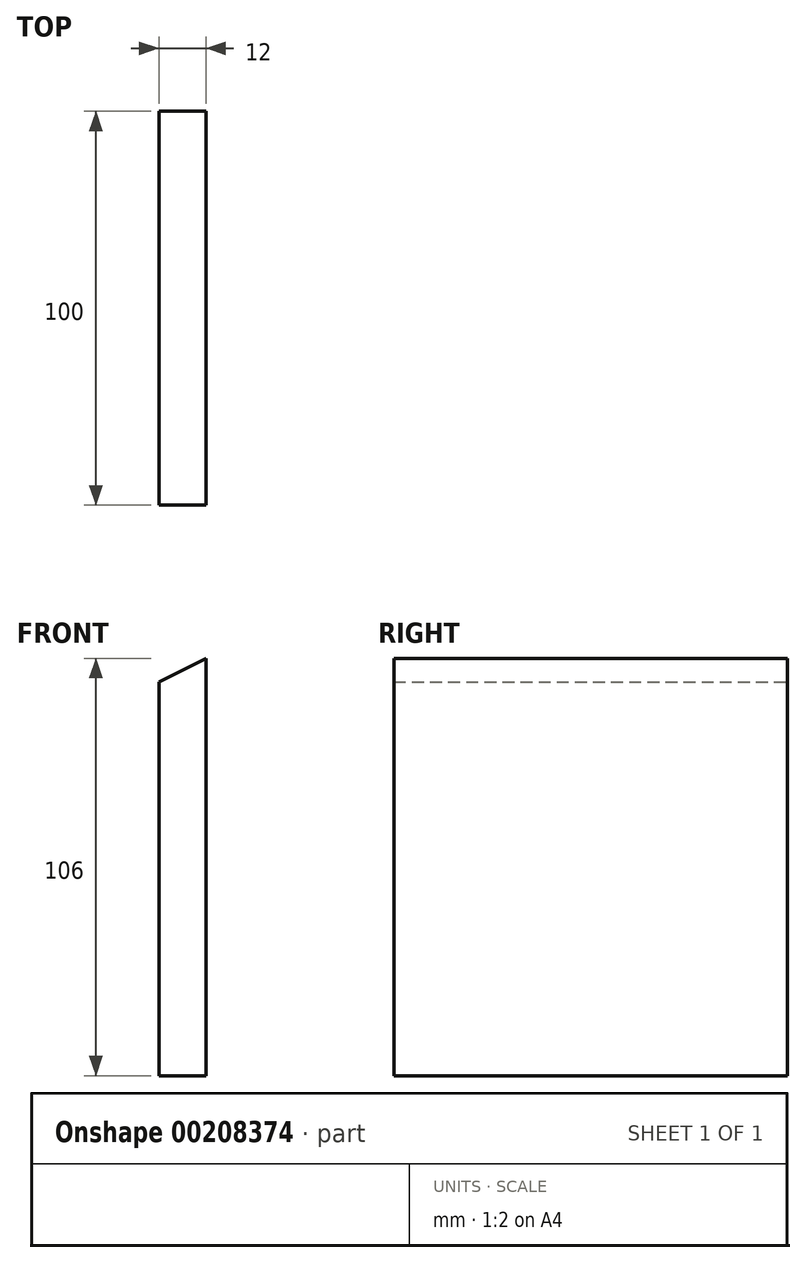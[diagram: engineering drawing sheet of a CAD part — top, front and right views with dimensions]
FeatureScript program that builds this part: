
annotation { "Feature Type Name" : "Feature", "Feature Type Description" : "" }
export const myFeature = defineFeature(function(context is Context, id is Id, definition is map)
    precondition{}
    {
        {
            var Q0;
            Q0=qCreatedBy(makeId("Front.planeOp"),FACE);
            var sketch = newSketch(context, id + "F0", { "sketchPlane" : qUnion([Q0])});
            skLineSegment(sketch, "E0.bottom", {"start": v(0, 0) * mm, "end": v(12, 0) * mm});
            skLineSegment(sketch, "E0.left", {"start": v(0, 0) * mm, "end": v(0, 100) * mm});
            skLineSegment(sketch, "E1", {"start": v(100, 100) * mm, "end": v(100, 150) * mm});
            skLineSegment(sketch, "E2", {"start": v(12, 106) * mm, "end": v(0, 100) * mm});
            skLineSegment(sketch, "E3", {"start": v(12, 106) * mm, "end": v(12, 0) * mm});
            skPoint(sketch, "E3.endSnap0", {"position": v(10, 0) * mm});
            skPoint(sketch, "E4.orphan", {"position": v(20, 0) * mm});
            skSolve(sketch);
        }
        {
            var Q0;
            Q0=makeQuery(id+"F0.imprint","IMPRINT",FACE,{"disambiguationData":[TD([[makeQuery(id+"F0.imprint","IMPRINT",EDGE,{"derivedFrom":sQuery(id+"F0.wireOp",EDGE,"E0.bottom")}),1.0]])]});
            extrude(context, id + "F1", {"entities" : qUnion([Q0]), "depth" : 100 * mm});
        }
    });
